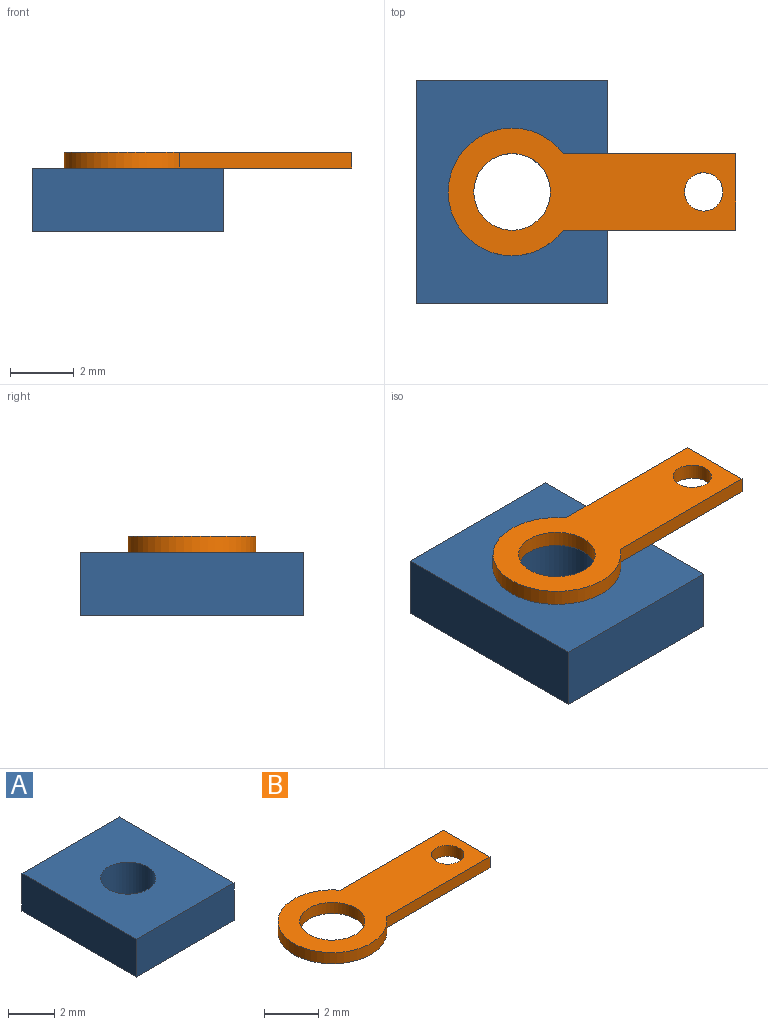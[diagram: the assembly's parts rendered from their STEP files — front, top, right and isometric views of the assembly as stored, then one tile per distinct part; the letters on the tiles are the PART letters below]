
ASSEMBLY  parts=2 mates=1
PART A: 7 faces, bbox 6x7x2 mm
  f0: plane 7x2mm, normal (1,0,0), area 14mm2, adj f1,f3,f4,f5
  f1: plane 6x2mm, normal (0,1,0), area 12mm2, adj f0,f2,f4,f5
  f2: plane 7x2mm, normal (-1,0,0), area 14mm2, adj f1,f3,f4,f5
  f3: plane 6x2mm, normal (0,-1,0), area 12mm2, adj f0,f2,f4,f5
  f4: plane 7x6mm, normal (0,0,1), area 37.5mm2, adj f0,f1,f2,f3,f6
  f5: plane 7x6mm, normal (0,0,-1), area 37.5mm2, adj f0,f1,f2,f3,f6
  f6: cylinder r=1.2mm len=2.4mm, axis (0,0,1), area 15.1mm2, adj f4,f5
PART B: 8 faces, bbox 9x4x0.5 mm
  f0: cylinder r=2mm len=4mm, axis (0,0,-1), area 5mm2, adj f1,f2,f4,f5
  f1: plane 9x4mm, normal (0,0,1), area 19.2mm2, adj f0,f3,f4,f5,f6,f7
  f2: plane 9x4mm, normal (0,0,-1), area 19.2mm2, adj f0,f3,f4,f5,f6,f7
  f3: cylinder r=1.2mm len=2.4mm, axis (0,0,1), area 3.8mm2, adj f1,f2
  f4: plane 5.4x0.5mm, normal (0,1,0), area 2.7mm2, adj f0,f1,f2,f6
  f5: plane 5.4x0.5mm, normal (0,-1,0), area 2.7mm2, adj f0,f1,f2,f6
  f6: plane 2.4x0.5mm, normal (1,0,0), area 1.2mm2, adj f1,f2,f4,f5
  f7: cylinder r=0.6mm len=1.2mm, axis (0,0,1), area 1.9mm2, adj f1,f2
PLACE A t=(3.23,4.54,-2.51)mm
PLACE B t=(3.23,4.54,-0.51)mm
MATE planar B.f2 <-> A.f6  axis (0,0,-1) through (5.72,4.54,-0.51)mm
